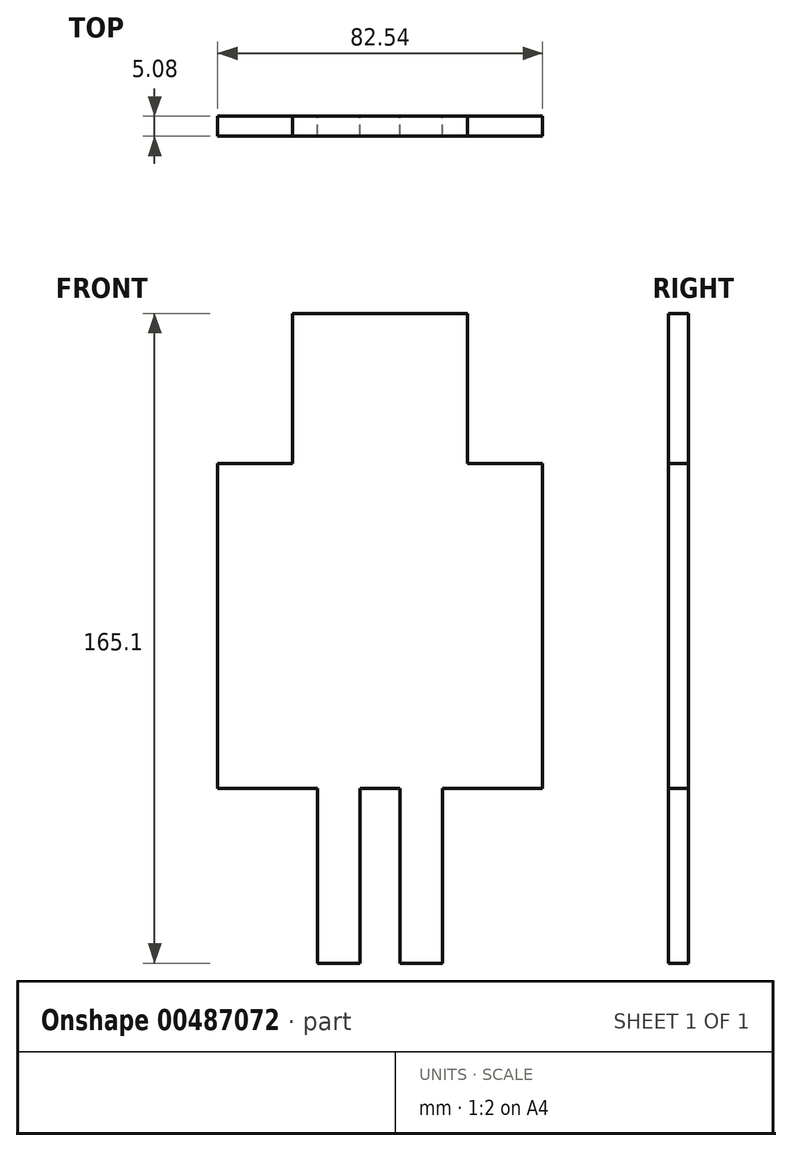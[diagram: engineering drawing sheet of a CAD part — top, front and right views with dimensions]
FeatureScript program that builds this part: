
annotation { "Feature Type Name" : "Feature", "Feature Type Description" : "" }
export const myFeature = defineFeature(function(context is Context, id is Id, definition is map)
    precondition{}
    {
        {
            var Q0;
            Q0=qCreatedBy(makeId("Front.planeOp"),FACE);
            var sketch = newSketch(context, id + "F0", { "sketchPlane" : qUnion([Q0])});
            skLineSegment(sketch, "E0.bottom", {"start": v(41.28, -43.4) * mm, "end": v(15.87, -43.4) * mm});
            skLineSegment(sketch, "E0.top", {"start": v(41.28, 39.15) * mm, "end": v(22.22, 39.15) * mm});
            skLineSegment(sketch, "E0.left", {"start": v(41.28, -43.4) * mm, "end": v(41.28, 39.15) * mm});
            skLineSegment(sketch, "E0.right", {"start": v(-41.28, -43.4) * mm, "end": v(-41.28, 39.15) * mm});
            skPoint(sketch, "E0.middle", {"position": v(0, -2.12) * mm});
            skLineSegment(sketch, "E1.top", {"start": v(-15.88, -87.85) * mm, "end": v(-5.08, -87.85) * mm});
            skLineSegment(sketch, "E1.left", {"start": v(-15.88, -43.4) * mm, "end": v(-15.88, -87.85) * mm});
            skLineSegment(sketch, "E1.right", {"start": v(-5.08, -43.4) * mm, "end": v(-5.08, -87.85) * mm});
            skLineSegment(sketch, "E2.trimOffspring", {"start": v(-15.88, -43.4) * mm, "end": v(-41.28, -43.4) * mm});
            skLineSegment(sketch, "E3.top", {"start": v(5.08, -87.85) * mm, "end": v(15.88, -87.85) * mm});
            skLineSegment(sketch, "E3.left", {"start": v(5.08, -43.4) * mm, "end": v(5.08, -87.85) * mm});
            skLineSegment(sketch, "E3.right", {"start": v(15.88, -43.4) * mm, "end": v(15.88, -87.85) * mm});
            skLineSegment(sketch, "E4.trimOffspring", {"start": v(5.08, -43.4) * mm, "end": v(-5.08, -43.4) * mm});
            skLineSegment(sketch, "E5.top", {"start": v(-22.23, 77.25) * mm, "end": v(22.22, 77.25) * mm});
            skLineSegment(sketch, "E5.left", {"start": v(-22.23, 39.15) * mm, "end": v(-22.23, 77.25) * mm});
            skLineSegment(sketch, "E5.right", {"start": v(22.22, 39.15) * mm, "end": v(22.22, 77.25) * mm});
            skLineSegment(sketch, "E6.trimOffspring", {"start": v(-22.23, 39.15) * mm, "end": v(-41.28, 39.15) * mm});
            skSolve(sketch);
        }
        {
            var Q0;
            Q0=makeQuery(id+"F0.imprint","IMPRINT",FACE,{"disambiguationData":[TD([[makeQuery(id+"F0.imprint","IMPRINT",EDGE,{"derivedFrom":sQuery(id+"F0.wireOp",EDGE,"E0.bottom")}),-1.0]])]});
            extrude(context, id + "F1", {"entities" : qUnion([Q0]), "depth" : 5.08 * mm});
        }
    });
